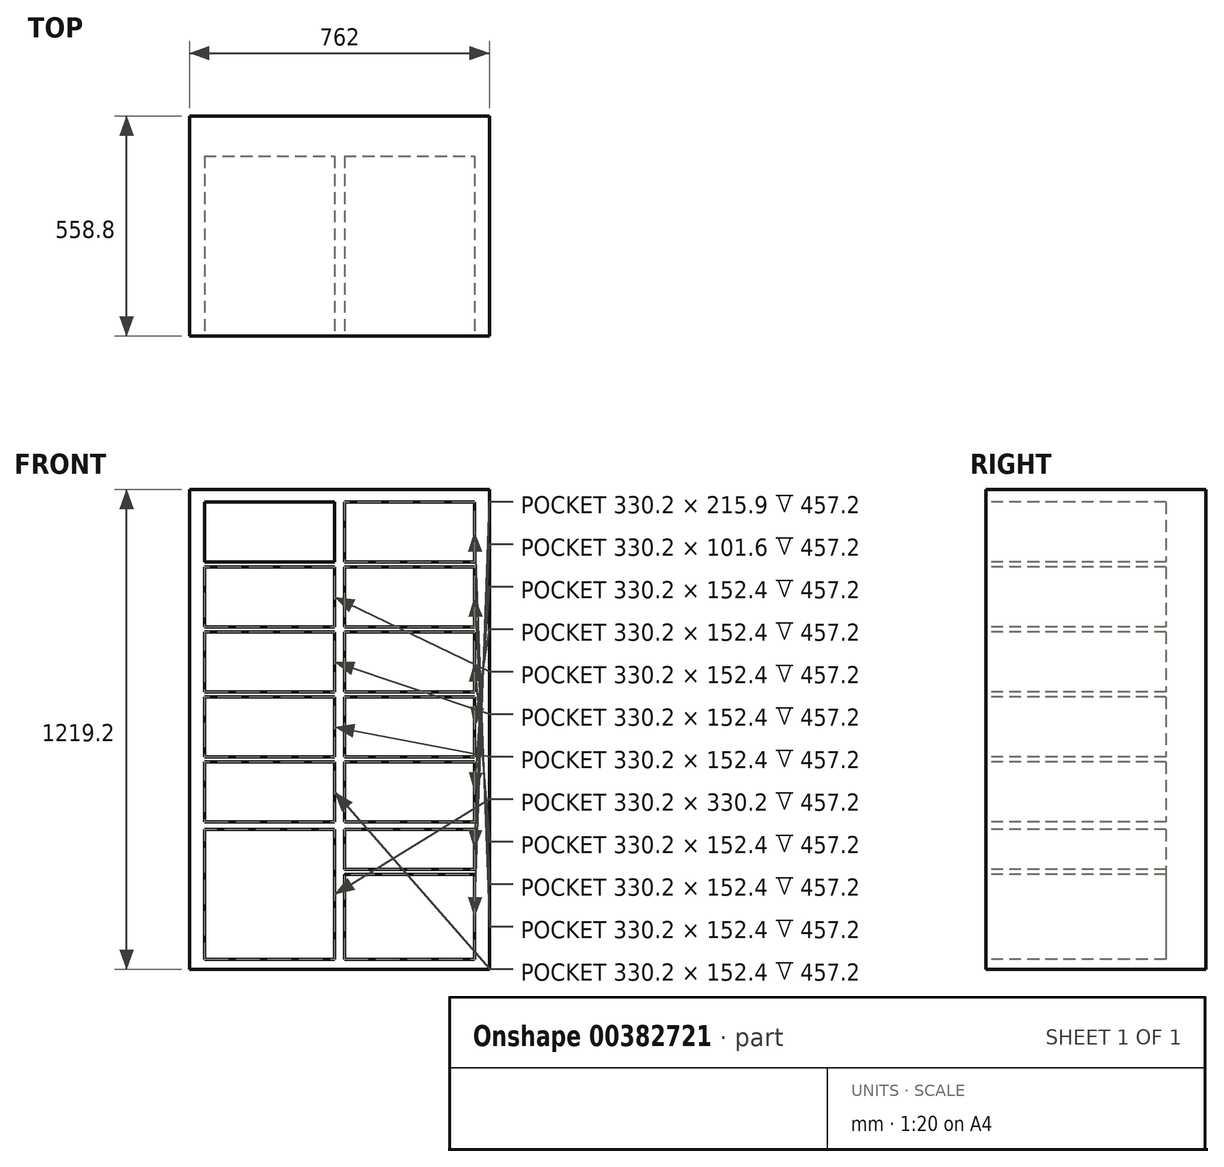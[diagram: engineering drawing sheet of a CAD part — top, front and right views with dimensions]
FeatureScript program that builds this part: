
annotation { "Feature Type Name" : "Feature", "Feature Type Description" : "" }
export const myFeature = defineFeature(function(context is Context, id is Id, definition is map)
    precondition{}
    {
        {
            var Q0;
            Q0=qCreatedBy(makeId("Front.planeOp"),FACE);
            var sketch = newSketch(context, id + "F0", { "sketchPlane" : qUnion([Q0])});
            skLineSegment(sketch, "E0.bottom", {"start": v(-599.32, -584.28) * mm, "end": v(162.68, -584.28) * mm});
            skLineSegment(sketch, "E0.top", {"start": v(-599.32, 634.92) * mm, "end": v(162.68, 634.92) * mm});
            skLineSegment(sketch, "E0.left", {"start": v(-599.32, -584.28) * mm, "end": v(-599.32, 634.92) * mm});
            skLineSegment(sketch, "E0.right", {"start": v(162.68, -584.28) * mm, "end": v(162.68, 634.92) * mm});
            skSolve(sketch);
        }
        {
            var Q0;
            Q0 = qSketchRegion(id + "F0", true);
            extrude(context, id + "F1", {"entities" : qUnion([Q0]), "depth" : 558.8 * mm});
        }
        {
            var Q0;
            Q0=makeQuery(id+"F1.opExtrude","CAP_FACE",FACE,{"disambiguationData":[OSD([sQuery(id+"F0.wireOp",EDGE,"E0.bottom"),sQuery(id+"F0.wireOp",EDGE,"E0.top"),sQuery(id+"F0.wireOp",EDGE,"E0.left"),sQuery(id+"F0.wireOp",EDGE,"E0.right")])],"isStart":false});
            var sketch = newSketch(context, id + "F2", { "sketchPlane" : qUnion([Q0])});
            skLineSegment(sketch, "E1.bottom", {"start": v(-561.22, 603.17) * mm, "end": v(-231.02, 603.17) * mm});
            skLineSegment(sketch, "E1.top", {"start": v(-561.22, 450.77) * mm, "end": v(-231.02, 450.77) * mm});
            skLineSegment(sketch, "E1.left", {"start": v(-561.22, 603.17) * mm, "end": v(-561.22, 450.77) * mm});
            skLineSegment(sketch, "E1.right", {"start": v(-231.02, 603.17) * mm, "end": v(-231.02, 450.77) * mm});
            skLineSegment(sketch, "E2.0.1.0", {"start": v(-561.22, 438.07) * mm, "end": v(-561.22, 285.67) * mm});
            skLineSegment(sketch, "E2.0.1.1", {"start": v(-561.22, 438.07) * mm, "end": v(-231.02, 438.07) * mm});
            skLineSegment(sketch, "E2.0.1.2", {"start": v(-561.22, 285.67) * mm, "end": v(-231.02, 285.67) * mm});
            skLineSegment(sketch, "E2.0.1.3", {"start": v(-231.02, 438.07) * mm, "end": v(-231.02, 285.67) * mm});
            skLineSegment(sketch, "E2.0.2.0", {"start": v(-561.22, 272.97) * mm, "end": v(-561.22, 120.57) * mm});
            skLineSegment(sketch, "E2.0.2.1", {"start": v(-561.22, 272.97) * mm, "end": v(-231.02, 272.97) * mm});
            skLineSegment(sketch, "E2.0.2.2", {"start": v(-561.22, 120.57) * mm, "end": v(-231.02, 120.57) * mm});
            skLineSegment(sketch, "E2.0.2.3", {"start": v(-231.02, 272.97) * mm, "end": v(-231.02, 120.57) * mm});
            skLineSegment(sketch, "E2.0.3.0", {"start": v(-561.22, 107.87) * mm, "end": v(-561.22, -44.53) * mm});
            skLineSegment(sketch, "E2.0.3.1", {"start": v(-561.22, 107.87) * mm, "end": v(-231.02, 107.87) * mm});
            skLineSegment(sketch, "E2.0.3.2", {"start": v(-561.22, -44.53) * mm, "end": v(-231.02, -44.53) * mm});
            skLineSegment(sketch, "E2.0.3.3", {"start": v(-231.02, 107.87) * mm, "end": v(-231.02, -44.53) * mm});
            skLineSegment(sketch, "E2.direction1", {"start": v(-561.22, 450.77) * mm, "end": v(-205.62, 450.77) * mm, "construction": true});
            skLineSegment(sketch, "E2.direction2", {"start": v(-561.22, 450.77) * mm, "end": v(-561.22, 285.67) * mm, "construction": true});
            skLineSegment(sketch, "E3.bottom", {"start": v(-561.22, -228.83) * mm, "end": v(-231.02, -228.83) * mm});
            skLineSegment(sketch, "E3.top", {"start": v(-561.22, -559.03) * mm, "end": v(-231.02, -559.03) * mm});
            skLineSegment(sketch, "E3.left", {"start": v(-561.22, -228.83) * mm, "end": v(-561.22, -559.03) * mm});
            skLineSegment(sketch, "E3.right", {"start": v(-231.02, -228.83) * mm, "end": v(-231.02, -559.03) * mm});
            skLineSegment(sketch, "E4.0.0.4", {"start": v(-561.22, -57.23) * mm, "end": v(-561.22, -209.63) * mm});
            skLineSegment(sketch, "E4.3.0.4", {"start": v(-561.22, -57.23) * mm, "end": v(-231.02, -57.23) * mm});
            skLineSegment(sketch, "E4.6.0.4", {"start": v(-561.22, -209.63) * mm, "end": v(-231.02, -209.63) * mm});
            skLineSegment(sketch, "E4.9.0.4", {"start": v(-231.02, -57.23) * mm, "end": v(-231.02, -209.63) * mm});
            skLineSegment(sketch, "E5.0.1.0", {"start": v(-205.62, 603.17) * mm, "end": v(-205.62, 450.77) * mm});
            skLineSegment(sketch, "E5.3.1.0", {"start": v(-205.62, 603.17) * mm, "end": v(124.58, 603.17) * mm});
            skLineSegment(sketch, "E5.6.1.0", {"start": v(-205.62, 450.77) * mm, "end": v(124.58, 450.77) * mm});
            skLineSegment(sketch, "E5.9.1.0", {"start": v(124.58, 603.17) * mm, "end": v(124.58, 450.77) * mm});
            skLineSegment(sketch, "E5.0.1.1", {"start": v(-205.62, 438.07) * mm, "end": v(-205.62, 285.67) * mm});
            skLineSegment(sketch, "E5.3.1.1", {"start": v(-205.62, 438.07) * mm, "end": v(124.58, 438.07) * mm});
            skLineSegment(sketch, "E5.6.1.1", {"start": v(-205.62, 285.67) * mm, "end": v(124.58, 285.67) * mm});
            skLineSegment(sketch, "E5.9.1.1", {"start": v(124.58, 438.07) * mm, "end": v(124.58, 285.67) * mm});
            skLineSegment(sketch, "E5.0.1.2", {"start": v(-205.62, 272.97) * mm, "end": v(-205.62, 120.57) * mm});
            skLineSegment(sketch, "E5.3.1.2", {"start": v(-205.62, 272.97) * mm, "end": v(124.58, 272.97) * mm});
            skLineSegment(sketch, "E5.6.1.2", {"start": v(-205.62, 120.57) * mm, "end": v(124.58, 120.57) * mm});
            skLineSegment(sketch, "E5.9.1.2", {"start": v(124.58, 272.97) * mm, "end": v(124.58, 120.57) * mm});
            skLineSegment(sketch, "E5.0.1.3", {"start": v(-205.62, 107.87) * mm, "end": v(-205.62, -44.53) * mm});
            skLineSegment(sketch, "E5.3.1.3", {"start": v(-205.62, 107.87) * mm, "end": v(124.58, 107.87) * mm});
            skLineSegment(sketch, "E5.6.1.3", {"start": v(-205.62, -44.53) * mm, "end": v(124.58, -44.53) * mm});
            skLineSegment(sketch, "E5.9.1.3", {"start": v(124.58, 107.87) * mm, "end": v(124.58, -44.53) * mm});
            skLineSegment(sketch, "E5.0.1.4", {"start": v(-205.62, -57.23) * mm, "end": v(-205.62, -209.63) * mm});
            skLineSegment(sketch, "E5.3.1.4", {"start": v(-205.62, -57.23) * mm, "end": v(124.58, -57.23) * mm});
            skLineSegment(sketch, "E5.6.1.4", {"start": v(-205.62, -209.63) * mm, "end": v(124.58, -209.63) * mm});
            skLineSegment(sketch, "E5.9.1.4", {"start": v(124.58, -57.23) * mm, "end": v(124.58, -209.63) * mm});
            skLineSegment(sketch, "E6.bottom", {"start": v(-205.62, -228.83) * mm, "end": v(124.58, -228.83) * mm});
            skLineSegment(sketch, "E6.top", {"start": v(-205.62, -330.43) * mm, "end": v(124.58, -330.43) * mm});
            skLineSegment(sketch, "E6.left", {"start": v(-205.62, -228.83) * mm, "end": v(-205.62, -330.43) * mm});
            skLineSegment(sketch, "E6.right", {"start": v(124.58, -228.83) * mm, "end": v(124.58, -330.43) * mm});
            skLineSegment(sketch, "E7.bottom", {"start": v(-205.62, -343.13) * mm, "end": v(124.58, -343.13) * mm});
            skLineSegment(sketch, "E7.top", {"start": v(-205.62, -559.03) * mm, "end": v(124.58, -559.03) * mm});
            skLineSegment(sketch, "E7.left", {"start": v(-205.62, -343.13) * mm, "end": v(-205.62, -559.03) * mm});
            skLineSegment(sketch, "E7.right", {"start": v(124.58, -343.13) * mm, "end": v(124.58, -559.03) * mm});
            skSolve(sketch);
        }
        {
            var Q0;
            Q0 = qSketchRegion(id + "F2", true);
            extrude(context, id + "F3", {"entities" : qUnion([Q0]), "operationType" : NewBodyOperationType.REMOVE, "oppositeDirection" : true, "depth" : 457.2 * mm});
        }
    });
